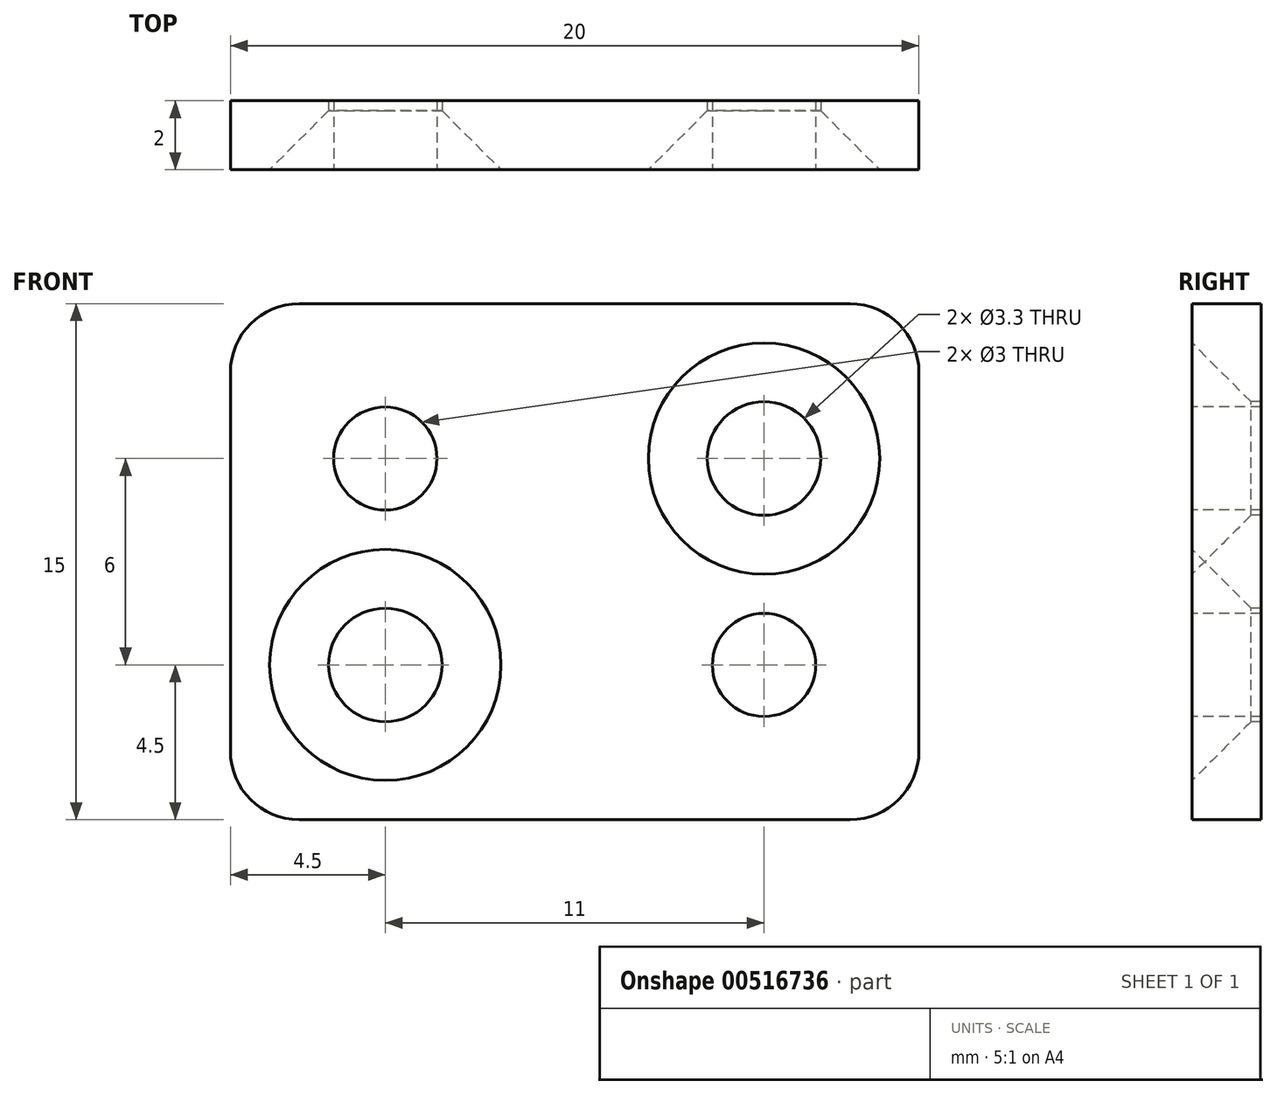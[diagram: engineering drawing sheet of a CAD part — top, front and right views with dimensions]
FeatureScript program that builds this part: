
annotation { "Feature Type Name" : "Feature", "Feature Type Description" : "" }
export const myFeature = defineFeature(function(context is Context, id is Id, definition is map)
    precondition{}
    {
        {
            var Q0;
            Q0=qCreatedBy(makeId("Front.planeOp"),FACE);
            var sketch = newSketch(context, id + "F0", { "sketchPlane" : qUnion([Q0])});
            skLineSegment(sketch, "E0.bottom", {"start": v(0, 0) * mm, "end": v(20, 0) * mm});
            skLineSegment(sketch, "E0.top", {"start": v(0, 15) * mm, "end": v(20, 15) * mm});
            skLineSegment(sketch, "E0.left", {"start": v(0, 0) * mm, "end": v(0, 15) * mm});
            skLineSegment(sketch, "E0.right", {"start": v(20, 0) * mm, "end": v(20, 15) * mm});
            skSolve(sketch);
        }
        {
            var Q0;
            Q0 = qSketchRegion(id + "F0", true);
            extrude(context, id + "F1", {"entities" : qUnion([Q0]), "oppositeDirection" : true, "depth" : 2 * mm, "offsetDistance" : 25 * mm});
        }
        {
            var Q0;
            Q0=makeQuery(id+"F0.imprint","IMPRINT",FACE,{"disambiguationData":[TD([[makeQuery(id+"F0.imprint","IMPRINT",EDGE,{"derivedFrom":sQuery(id+"F0.wireOp",EDGE,"E0.bottom")}),1.0]])]});
            var sketch = newSketch(context, id + "F2", { "sketchPlane" : qUnion([Q0])});
            skLineSegment(sketch, "E1", {"start": v(10, 31.14) * mm, "end": v(10, -1.14) * mm, "construction": true});
            skPoint(sketch, "E2", {"position": v(4.5, 10.5) * mm});
            skPoint(sketch, "E3", {"position": v(4.5, 4.5) * mm});
            skPoint(sketch, "E4.MirrorP", {"position": v(15.5, 10.5) * mm});
            skPoint(sketch, "E5.MirrorP", {"position": v(15.5, 4.5) * mm});
            skSolve(sketch);
        }
        {
            var Q0;
            Q0=sQuery(id+"F2.wireOp",VERTEX,"E4.MirrorP");
            var Q1;
            Q1=sQuery(id+"F2.wireOp",VERTEX,"E3");
            var Q2;
            Q2=makeQuery(id+"F1.opExtrude","SWEPT_BODY",BODY,{"disambiguationData":[OSD([sQuery(id+"F0.wireOp",EDGE,"E0.bottom"),sQuery(id+"F0.wireOp",EDGE,"E0.top"),sQuery(id+"F0.wireOp",EDGE,"E0.left"),sQuery(id+"F0.wireOp",EDGE,"E0.right")])]});
            hole(context, id + "F3", {"style" : HoleStyle.C_SINK, "endStyle" : HoleEndStyle.THROUGH, "standardTappedOrClearance" : lookupTablePath({ "standard" : "ISO", "fit" : "Normal", "size" : "M3", "type" : "Clearance" }), "standardBlindInLast" : lookupTablePath({ "fit" : "Standard", "standard" : "ISO", "size" : "M3", "type" : "Clearance" }), "holeDiameter" : 3.3 * mm, "cSinkDiameter" : 6.72 * mm, "cSinkAngle" : 90 * degree, "isTappedThrough" : true, "tappedDepth" : 12 * mm, "tapClearance" : 3, "locations" : qUnion([Q0, Q1]), "scope" : qUnion([Q2])});
        }
        {
            var Q0;
            Q0=makeQuery(id+"F2.imprint","IMPRINT",FACE,{"disambiguationData":[TD([[makeQuery(id+"F2.imprint","IMPRINT",EDGE,{"derivedFrom":makeQuery(id+"F0.imprint","IMPRINT",EDGE,{"derivedFrom":sQuery(id+"F0.wireOp",EDGE,"E0.bottom")})}),1.0]])]});
            var sketch = newSketch(context, id + "F4", { "sketchPlane" : qUnion([Q0])});
            skCircle(sketch, "E6", {"center": v(15.5, 4.5) * mm, "radius": 1.5 * mm});
            skCircle(sketch, "E7", {"center": v(4.5, 10.5) * mm, "radius": 1.5 * mm});
            skSolve(sketch);
        }
        {
            var Q0;
            Q0 = qSketchRegion(id + "F4", true);
            extrude(context, id + "F5", {"entities" : qUnion([Q0]), "operationType" : NewBodyOperationType.REMOVE, "endBound" : BoundingType.THROUGH_ALL, "oppositeDirection" : true, "depth" : 25 * mm, "offsetDistance" : 25 * mm});
        }
        {
            var Q0;
            Q0=makeQuery(id+"F1.opExtrude","SWEPT_EDGE",EDGE,{"disambiguationData":[OSD([sQuery(id+"F0.wireOp",EDGE,"E0.top"),sQuery(id+"F0.wireOp",EDGE,"E0.right")])]});
            var Q1;
            Q1=makeQuery(id+"F1.opExtrude","SWEPT_EDGE",EDGE,{"disambiguationData":[OSD([sQuery(id+"F0.wireOp",EDGE,"E0.top"),sQuery(id+"F0.wireOp",EDGE,"E0.left")])]});
            var Q2;
            Q2=makeQuery(id+"F1.opExtrude","SWEPT_EDGE",EDGE,{"disambiguationData":[OSD([sQuery(id+"F0.wireOp",EDGE,"E0.bottom"),sQuery(id+"F0.wireOp",EDGE,"E0.right")])]});
            var Q3;
            Q3=makeQuery(id+"F1.opExtrude","SWEPT_EDGE",EDGE,{"disambiguationData":[OSD([sQuery(id+"F0.wireOp",EDGE,"E0.bottom"),sQuery(id+"F0.wireOp",EDGE,"E0.left")])]});
            fillet(context, id + "F6", {"entities" : qUnion([Q0, Q1, Q2, Q3]), "radius" : 2 * mm, "tangentPropagation" : true, "allowEdgeOverflow" : false});
        }
    });
